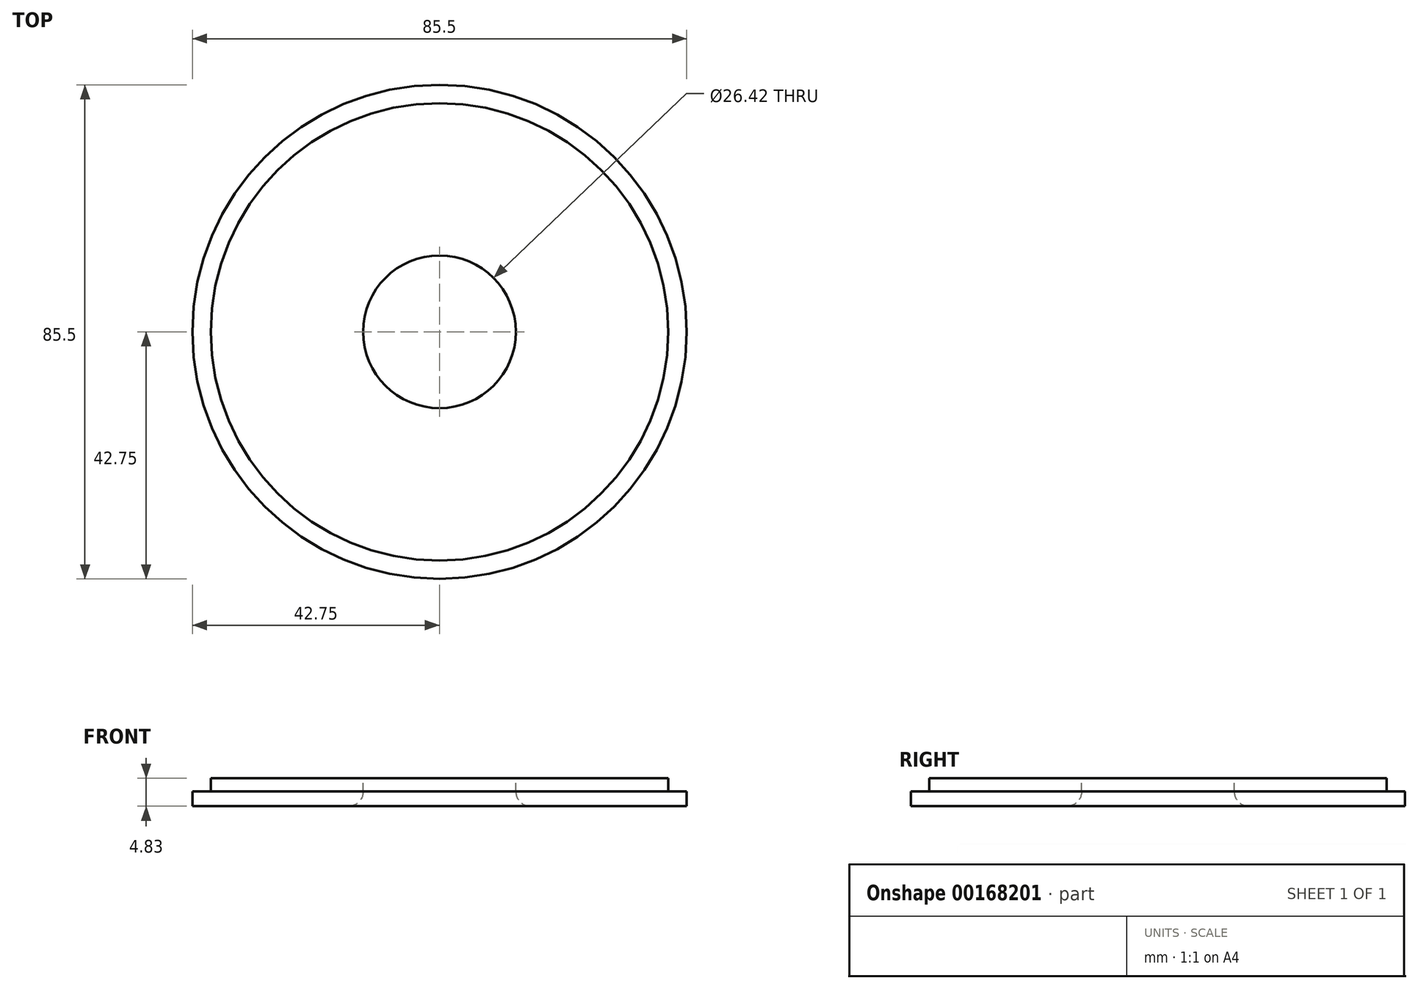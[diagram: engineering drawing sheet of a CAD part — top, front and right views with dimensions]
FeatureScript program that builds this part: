
annotation { "Feature Type Name" : "Feature", "Feature Type Description" : "" }
export const myFeature = defineFeature(function(context is Context, id is Id, definition is map)
    precondition{}
    {
        {
            var Q0;
            Q0=qCreatedBy(makeId("Top.planeOp"),FACE);
            var sketch = newSketch(context, id + "F0", { "sketchPlane" : qUnion([Q0])});
            skCircle(sketch, "E0", {"center": v(0, 0) * mm, "radius": 42.75 * mm});
            skSolve(sketch);
        }
        {
            var Q0;
            Q0 = qSketchRegion(id + "F0", true);
            extrude(context, id + "F1", {"entities" : qUnion([Q0]), "depth" : 2.54 * mm});
        }
        {
            var Q0;
            Q0=makeQuery(id+"F1.opExtrude","CAP_FACE",FACE,{"disambiguationData":[OSD([sQuery(id+"F0.wireOp",EDGE,"E0")])],"isStart":false});
            var sketch = newSketch(context, id + "F2", { "sketchPlane" : qUnion([Q0])});
            skCircle(sketch, "E1", {"center": v(0, 0) * mm, "radius": 39.57 * mm});
            skSolve(sketch);
        }
        {
            var Q0;
            Q0 = qSketchRegion(id + "F2", true);
            extrude(context, id + "F3", {"entities" : qUnion([Q0]), "operationType" : NewBodyOperationType.ADD, "depth" : 2.3 * mm});
        }
        {
            var Q0;
            Q0=makeQuery(id+"F3.opExtrude","CAP_FACE",FACE,{"disambiguationData":[OSD([sQuery(id+"F2.wireOp",EDGE,"E1")])],"isStart":false});
            var sketch = newSketch(context, id + "F4", { "sketchPlane" : qUnion([Q0])});
            skCircle(sketch, "E2", {"center": v(0, 0) * mm, "radius": 13.2 * mm});
            skSolve(sketch);
        }
        {
            var Q0;
            Q0 = qSketchRegion(id + "F4", true);
            extrude(context, id + "F5", {"entities" : qUnion([Q0]), "operationType" : NewBodyOperationType.REMOVE, "endBound" : BoundingType.THROUGH_ALL, "oppositeDirection" : true, "depth" : 25.4 * mm});
        }
        {
            var Q0;
            Q0=makeQuery(id+"F5.boolean.opBoolean","INTERSECT",EDGE,{"derivedFrom":[makeQuery(id+"F1.opExtrude","CAP_FACE",FACE,{"disambiguationData":[OSD([sQuery(id+"F0.wireOp",EDGE,"E0")])],"isStart":true}),makeQuery(id+"F5.opExtrude","SWEPT_FACE",FACE,{"disambiguationData":[OSD([sQuery(id+"F4.wireOp",EDGE,"E2")])]})]});
            fillet(context, id + "F6", {"entities" : qUnion([Q0]), "radius" : 2.54 * mm, "tangentPropagation" : true, "allowEdgeOverflow" : false});
        }
    });
